# Revit family: OFM LED FLUSH MOUNT LIGHT
name_source: partatom
category: Lighting Fixtures
units: mm (PartAtom-declared; Revit-internal decimal feet)

## family parameters
Cut with Voids When Loaded = No
Host = Face
Light Source = Yes
Part Type = Normal
Room Calculation Point = No
Round Connector Dimension = Use Diameter
Shared = No

## types (2) — shared parameters
Apparent Load = 23 VA
Average life based on 77F(HRS) = 50000
CRI = 80
Color Filter = 16777215
Default Elevation = 4' - 0"
Description = The OFM outdoor flush mount light comes in round and square shapes. Body and bracket in die-cast 
aluminum. Powder coated with pretreatment plus silicon rubber gasket for outdoor use. Simple and elegant 
appearanceis ideal for general illumination for residential and commercial applications such as porches, 
covered walkways and store entrances.
Dimming Lamp Color Temperature Shift = <None>
Finish/Color = White
IP Rating = 20
Inside Bulb Element = BULB Material
Manufacturer = Above All Lighting
Tilt Angle = -90.00°
Type Comments = OFM LED FLUSH MOUNT LIGHT
URL = https://www.abovealllighting.com
Voltage = 120 V
WATTS = 18 W

## per-type parameters (varying)
| type | Fixture Diameter | Fixture Height | Light Source Height | Order number | Photometric Web File | Round Light | Square Light |
| OFMR18304-WH | 0' - 9 27/32" | 0' - 2 11/16" | 0' - 3" | 16011 | OFMR18304-WH.IES | Yes | No |
| OFMS18304-WH | 0' - 9 9/32" | 0' - 2 23/32" | 0' - 3 1/32" | 16012 | OFMS18304-WH.IES | No | Yes |

note: column(s) folded — value = type name in every type: Model

## geometry (parser evidence)
native form markers: Sweep x7
no freeform markers — native parametric forms only
